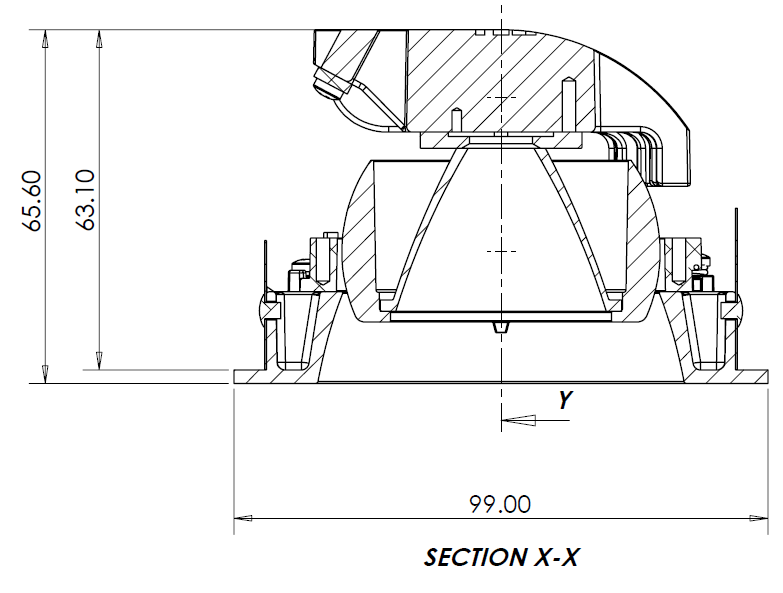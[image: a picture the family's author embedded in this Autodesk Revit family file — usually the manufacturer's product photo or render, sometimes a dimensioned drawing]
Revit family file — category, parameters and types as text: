
# Revit family: Trimless-Ambiance-X80-Wallwasher
name_source: partatom
category: Lighting Fixtures
revit_build: Autodesk Revit MEP 2014 (Build: 20130308_1515(x64)
units: mm (PartAtom-declared; Revit-internal decimal feet)

## types (1)
- Trimless Ambiance X80 Wallwasher
    Aperture (mm) = 80
    Apparent Load = 20 VA
    CRI = 80
    Color Filter = 16777215
    Colour temperature (K) = 2700 / 3000 / 3500 / 4000
    Cut Out (mm) = 100
    Description = Recessed LED Trimless Round Wallwasher
    Dimension (mm) = 80
    Dimming Lamp Color Temperature Shift = <None>
    Height (mm) = 108
    Lamp = LED
    Luminous flux of luminaire (lm) = Up to 2000 lumens
    Manufacturer = Designed Architectural Lighting
    Model = Trimless Ambiance X80 Wallwasher
    Photometric Web File = G2204.ies
    Tilt Angle = 60.00°
    Type = Recessed Downlighter
    Type Comments = Recessed
    Wattage Comments = 19.5

## geometry (parser evidence)
native form markers: Sweep x1
no freeform markers — native parametric forms only
